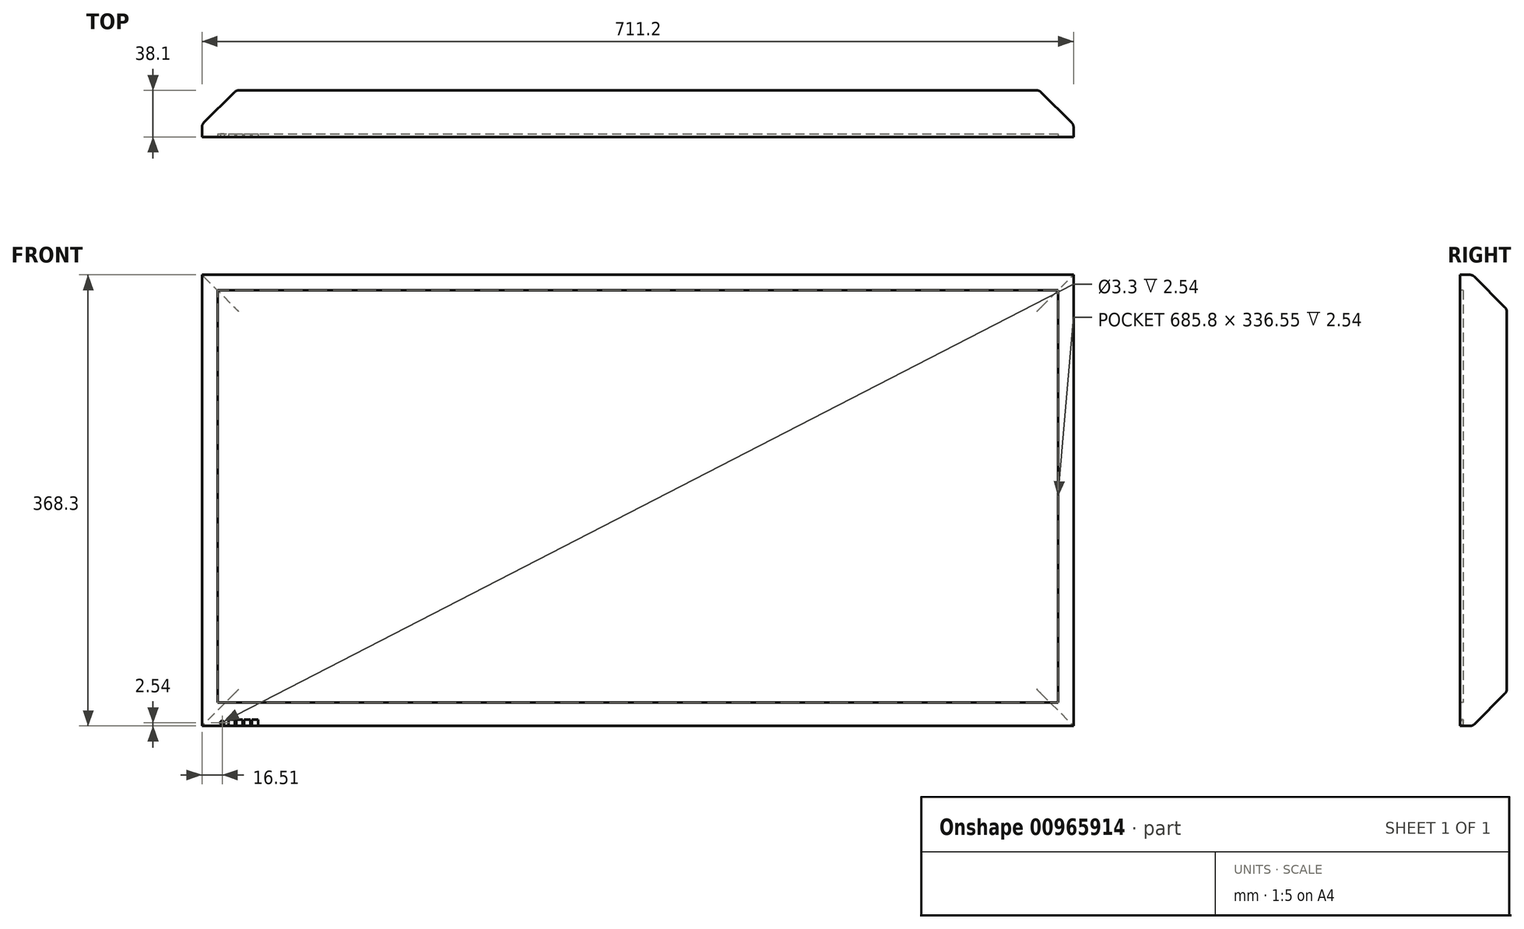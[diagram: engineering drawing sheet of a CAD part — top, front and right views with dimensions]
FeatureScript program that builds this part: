
annotation { "Feature Type Name" : "Feature", "Feature Type Description" : "" }
export const myFeature = defineFeature(function(context is Context, id is Id, definition is map)
    precondition{}
    {
        {
            var Q0;
            Q0=qCreatedBy(makeId("Front.planeOp"),FACE);
            var sketch = newSketch(context, id + "F0", { "sketchPlane" : qUnion([Q0])});
            skLineSegment(sketch, "E0.bottom", {"start": v(0, 0) * mm, "end": v(711.2, 0) * mm});
            skLineSegment(sketch, "E0.top", {"start": v(0, -368.3) * mm, "end": v(711.2, -368.3) * mm});
            skLineSegment(sketch, "E0.left", {"start": v(0, 0) * mm, "end": v(0, -368.3) * mm});
            skLineSegment(sketch, "E0.right", {"start": v(711.2, 0) * mm, "end": v(711.2, -368.3) * mm});
            skSolve(sketch);
        }
        {
            var Q0;
            Q0=qSketchRegion(id+"F0",true);
            extrude(context, id + "F1", {"entities" : qUnion([Q0]), "depth" : 38.1 * mm, "offsetDistance" : 25.4 * mm});
        }
        {
            var Q0;
            Q0=makeQuery(id+"F1.opExtrude","CAP_FACE",FACE,{"disambiguationData":[OSD([sQuery(id+"F0.wireOp",EDGE,"E0.bottom"),sQuery(id+"F0.wireOp",EDGE,"E0.top"),sQuery(id+"F0.wireOp",EDGE,"E0.left"),sQuery(id+"F0.wireOp",EDGE,"E0.right")])],"isStart":false});
            var sketch = newSketch(context, id + "F2", { "sketchPlane" : qUnion([Q0])});
            skLineSegment(sketch, "E1.bottom", {"start": v(12.7, -12.7) * mm, "end": v(698.5, -12.7) * mm});
            skLineSegment(sketch, "E1.top", {"start": v(12.7, -349.25) * mm, "end": v(698.5, -349.25) * mm});
            skLineSegment(sketch, "E1.left", {"start": v(12.7, -12.7) * mm, "end": v(12.7, -349.25) * mm});
            skLineSegment(sketch, "E1.right", {"start": v(698.5, -12.7) * mm, "end": v(698.5, -349.25) * mm});
            skSolve(sketch);
        }
        {
            var Q0;
            Q0=qSketchRegion(id+"F2",true);
            extrude(context, id + "F3", {"entities" : qUnion([Q0]), "operationType" : NewBodyOperationType.REMOVE, "oppositeDirection" : true, "depth" : 2.54 * mm, "offsetDistance" : 25.4 * mm});
        }
        {
            var Q0;
            Q0=makeQuery(id+"F1.opExtrude","CAP_FACE",FACE,{"disambiguationData":[OSD([sQuery(id+"F0.wireOp",EDGE,"E0.bottom"),sQuery(id+"F0.wireOp",EDGE,"E0.top"),sQuery(id+"F0.wireOp",EDGE,"E0.left"),sQuery(id+"F0.wireOp",EDGE,"E0.right")])],"isStart":false});
            var sketch = newSketch(context, id + "F4", { "sketchPlane" : qUnion([Q0])});
            skLineSegment(sketch, "E2", {"start": v(12.7, -349.25) * mm, "end": v(12.7, -368.3) * mm});
            skLineSegment(sketch, "E3", {"start": v(12.7, -368.3) * mm, "end": v(12.7, -363.22) * mm});
            skLineSegment(sketch, "E4", {"start": v(12.7, -363.22) * mm, "end": v(20.32, -363.22) * mm});
            skLineSegment(sketch, "E5", {"start": v(20.32, -363.22) * mm, "end": v(20.32, -368.3) * mm});
            skLineSegment(sketch, "E6", {"start": v(20.32, -363.22) * mm, "end": v(21.6, -363.22) * mm});
            skLineSegment(sketch, "E7", {"start": v(21.6, -363.22) * mm, "end": v(21.6, -368.3) * mm});
            skLineSegment(sketch, "E8", {"start": v(21.6, -363.22) * mm, "end": v(26.67, -363.22) * mm});
            skLineSegment(sketch, "E9", {"start": v(26.67, -363.22) * mm, "end": v(26.67, -368.3) * mm});
            skLineSegment(sketch, "E10", {"start": v(26.67, -368.3) * mm, "end": v(21.6, -368.3) * mm});
            skLineSegment(sketch, "E11", {"start": v(26.67, -363.22) * mm, "end": v(27.94, -363.22) * mm});
            skLineSegment(sketch, "E12", {"start": v(27.94, -363.22) * mm, "end": v(33.02, -363.22) * mm});
            skLineSegment(sketch, "E13", {"start": v(33.02, -363.22) * mm, "end": v(33.02, -368.3) * mm});
            skLineSegment(sketch, "E14", {"start": v(27.94, -363.22) * mm, "end": v(27.94, -368.3) * mm});
            skLineSegment(sketch, "E15", {"start": v(33.02, -363.22) * mm, "end": v(34.3, -363.22) * mm});
            skLineSegment(sketch, "E16", {"start": v(34.3, -363.22) * mm, "end": v(39.37, -363.22) * mm});
            skLineSegment(sketch, "E17", {"start": v(39.37, -363.22) * mm, "end": v(39.37, -368.3) * mm});
            skLineSegment(sketch, "E18", {"start": v(34.3, -363.22) * mm, "end": v(34.3, -368.3) * mm});
            skLineSegment(sketch, "E19", {"start": v(39.37, -363.22) * mm, "end": v(40.64, -363.22) * mm});
            skLineSegment(sketch, "E20", {"start": v(40.64, -363.22) * mm, "end": v(45.72, -363.22) * mm});
            skLineSegment(sketch, "E21", {"start": v(45.72, -363.22) * mm, "end": v(45.72, -368.3) * mm});
            skLineSegment(sketch, "E22", {"start": v(40.64, -363.22) * mm, "end": v(40.64, -368.3) * mm});
            skLineSegment(sketch, "E23", {"start": v(40.64, -368.3) * mm, "end": v(45.72, -368.3) * mm});
            skLineSegment(sketch, "E24", {"start": v(34.3, -368.3) * mm, "end": v(39.37, -368.3) * mm});
            skLineSegment(sketch, "E25", {"start": v(27.94, -368.3) * mm, "end": v(33.02, -368.3) * mm});
            skLineSegment(sketch, "E26", {"start": v(21.6, -368.3) * mm, "end": v(26.67, -368.3) * mm});
            skCircle(sketch, "E27", {"center": v(16.51, -365.76) * mm, "radius": 1.65 * mm});
            skSolve(sketch);
        }
        {
            var Q0;
            Q0=qSketchRegion(id+"F4",true);
            extrude(context, id + "F5", {"entities" : qUnion([Q0]), "operationType" : NewBodyOperationType.REMOVE, "oppositeDirection" : true, "depth" : 2.54 * mm, "offsetDistance" : 25.4 * mm});
        }
        {
            var Q0;
            Q0=qSketchRegion(id+"F4",true);
            extrude(context, id + "F6", {"entities" : qUnion([Q0]), "operationType" : NewBodyOperationType.REMOVE, "oppositeDirection" : true, "depth" : 2.54 * mm, "offsetDistance" : 25.4 * mm});
        }
        {
            var Q0;
            Q0=makeQuery(id+"F1.opExtrude","CAP_EDGE",EDGE,{"disambiguationData":[OSD([sQuery(id+"F0.wireOp",EDGE,"E0.top")])],"isStart":true});
            var Q1;
            Q1=makeQuery(id+"F1.opExtrude","CAP_EDGE",EDGE,{"disambiguationData":[OSD([sQuery(id+"F0.wireOp",EDGE,"E0.left")])],"isStart":true});
            var Q2;
            Q2=makeQuery(id+"F1.opExtrude","CAP_EDGE",EDGE,{"disambiguationData":[OSD([sQuery(id+"F0.wireOp",EDGE,"E0.right")])],"isStart":true});
            var Q3;
            Q3=makeQuery(id+"F1.opExtrude","CAP_EDGE",EDGE,{"disambiguationData":[OSD([sQuery(id+"F0.wireOp",EDGE,"E0.bottom")])],"isStart":true});
            chamfer(context, id + "F7", {"entities" : qUnion([Q0, Q1, Q2, Q3]), "width" : 27.94 * mm, "tangentPropagation" : true});
        }
        {
            var Q0;
            {var subQ0=sQuery(id+"F0.wireOp",EDGE,"E0.right");Q0=makeQuery(id+"F7.opChamfer","BLEND_EDGE",EDGE,{"blendedFrom":[makeQuery(id+"F1.opExtrude","CAP_EDGE",EDGE,{"disambiguationData":[OSD([subQ0])],"isStart":true}),makeQuery(id+"F1.opExtrude","CAP_FACE",FACE,{"disambiguationData":[OSD([sQuery(id+"F0.wireOp",EDGE,"E0.bottom"),sQuery(id+"F0.wireOp",EDGE,"E0.top"),sQuery(id+"F0.wireOp",EDGE,"E0.left"),subQ0])],"isStart":true})],"blendedInto":[makeQuery(id+"F1.opExtrude","CAP_FACE",FACE,{"disambiguationData":[OSD([sQuery(id+"F0.wireOp",EDGE,"E0.bottom"),sQuery(id+"F0.wireOp",EDGE,"E0.top"),sQuery(id+"F0.wireOp",EDGE,"E0.left"),subQ0])],"isStart":true})]});}
            var Q1;
            {var subQ0=sQuery(id+"F0.wireOp",EDGE,"E0.top");Q1=makeQuery(id+"F7.opChamfer","BLEND_EDGE",EDGE,{"blendedFrom":[makeQuery(id+"F1.opExtrude","CAP_EDGE",EDGE,{"disambiguationData":[OSD([subQ0])],"isStart":true}),makeQuery(id+"F1.opExtrude","CAP_FACE",FACE,{"disambiguationData":[OSD([sQuery(id+"F0.wireOp",EDGE,"E0.bottom"),subQ0,sQuery(id+"F0.wireOp",EDGE,"E0.left"),sQuery(id+"F0.wireOp",EDGE,"E0.right")])],"isStart":true})],"blendedInto":[makeQuery(id+"F1.opExtrude","CAP_FACE",FACE,{"disambiguationData":[OSD([sQuery(id+"F0.wireOp",EDGE,"E0.bottom"),subQ0,sQuery(id+"F0.wireOp",EDGE,"E0.left"),sQuery(id+"F0.wireOp",EDGE,"E0.right")])],"isStart":true})]});}
            var Q2;
            {var subQ0=sQuery(id+"F0.wireOp",EDGE,"E0.left");Q2=makeQuery(id+"F7.opChamfer","BLEND_EDGE",EDGE,{"blendedFrom":[makeQuery(id+"F1.opExtrude","CAP_EDGE",EDGE,{"disambiguationData":[OSD([subQ0])],"isStart":true}),makeQuery(id+"F1.opExtrude","CAP_FACE",FACE,{"disambiguationData":[OSD([sQuery(id+"F0.wireOp",EDGE,"E0.bottom"),sQuery(id+"F0.wireOp",EDGE,"E0.top"),subQ0,sQuery(id+"F0.wireOp",EDGE,"E0.right")])],"isStart":true})],"blendedInto":[makeQuery(id+"F1.opExtrude","CAP_FACE",FACE,{"disambiguationData":[OSD([sQuery(id+"F0.wireOp",EDGE,"E0.bottom"),sQuery(id+"F0.wireOp",EDGE,"E0.top"),subQ0,sQuery(id+"F0.wireOp",EDGE,"E0.right")])],"isStart":true})]});}
            var Q3;
            {var subQ0=sQuery(id+"F0.wireOp",EDGE,"E0.bottom");Q3=makeQuery(id+"F7.opChamfer","BLEND_EDGE",EDGE,{"blendedFrom":[makeQuery(id+"F1.opExtrude","CAP_EDGE",EDGE,{"disambiguationData":[OSD([subQ0])],"isStart":true}),makeQuery(id+"F1.opExtrude","CAP_FACE",FACE,{"disambiguationData":[OSD([subQ0,sQuery(id+"F0.wireOp",EDGE,"E0.top"),sQuery(id+"F0.wireOp",EDGE,"E0.left"),sQuery(id+"F0.wireOp",EDGE,"E0.right")])],"isStart":true})],"blendedInto":[makeQuery(id+"F1.opExtrude","CAP_FACE",FACE,{"disambiguationData":[OSD([subQ0,sQuery(id+"F0.wireOp",EDGE,"E0.top"),sQuery(id+"F0.wireOp",EDGE,"E0.left"),sQuery(id+"F0.wireOp",EDGE,"E0.right")])],"isStart":true})]});}
            var Q4;
            {var subQ0=sQuery(id+"F0.wireOp",EDGE,"E0.right");Q4=makeQuery(id+"F7.opChamfer","BLEND_EDGE",EDGE,{"blendedFrom":[makeQuery(id+"F1.opExtrude","CAP_EDGE",EDGE,{"disambiguationData":[OSD([subQ0])],"isStart":true}),makeQuery(id+"F1.opExtrude","SWEPT_FACE",FACE,{"disambiguationData":[OSD([subQ0])]})],"blendedInto":[makeQuery(id+"F1.opExtrude","SWEPT_FACE",FACE,{"disambiguationData":[OSD([subQ0])]})]});}
            var Q5;
            {var subQ0=sQuery(id+"F0.wireOp",EDGE,"E0.bottom");Q5=makeQuery(id+"F7.opChamfer","BLEND_EDGE",EDGE,{"blendedFrom":[makeQuery(id+"F1.opExtrude","CAP_EDGE",EDGE,{"disambiguationData":[OSD([subQ0])],"isStart":true}),makeQuery(id+"F1.opExtrude","SWEPT_FACE",FACE,{"disambiguationData":[OSD([subQ0])]})],"blendedInto":[makeQuery(id+"F1.opExtrude","SWEPT_FACE",FACE,{"disambiguationData":[OSD([subQ0])]})]});}
            var Q6;
            {var subQ0=sQuery(id+"F0.wireOp",EDGE,"E0.top");Q6=makeQuery(id+"F7.opChamfer","BLEND_EDGE",EDGE,{"blendedFrom":[makeQuery(id+"F1.opExtrude","CAP_EDGE",EDGE,{"disambiguationData":[OSD([subQ0])],"isStart":true}),makeQuery(id+"F1.opExtrude","SWEPT_FACE",FACE,{"disambiguationData":[OSD([subQ0])]})],"blendedInto":[makeQuery(id+"F1.opExtrude","SWEPT_FACE",FACE,{"disambiguationData":[OSD([subQ0])]})]});}
            var Q7;
            {var subQ0=sQuery(id+"F0.wireOp",EDGE,"E0.left");Q7=makeQuery(id+"F7.opChamfer","BLEND_EDGE",EDGE,{"blendedFrom":[makeQuery(id+"F1.opExtrude","CAP_EDGE",EDGE,{"disambiguationData":[OSD([subQ0])],"isStart":true}),makeQuery(id+"F1.opExtrude","SWEPT_FACE",FACE,{"disambiguationData":[OSD([subQ0])]})],"blendedInto":[makeQuery(id+"F1.opExtrude","SWEPT_FACE",FACE,{"disambiguationData":[OSD([subQ0])]})]});}
            fillet(context, id + "F8", {"entities" : qUnion([Q0, Q1, Q2, Q3, Q4, Q5, Q6, Q7]), "tangentPropagation" : true, "radius" : 5.08 * mm, "defaultsChanged" : false, "vertexSettings" : [], "allowEdgeOverflow" : false});
        }
    });
